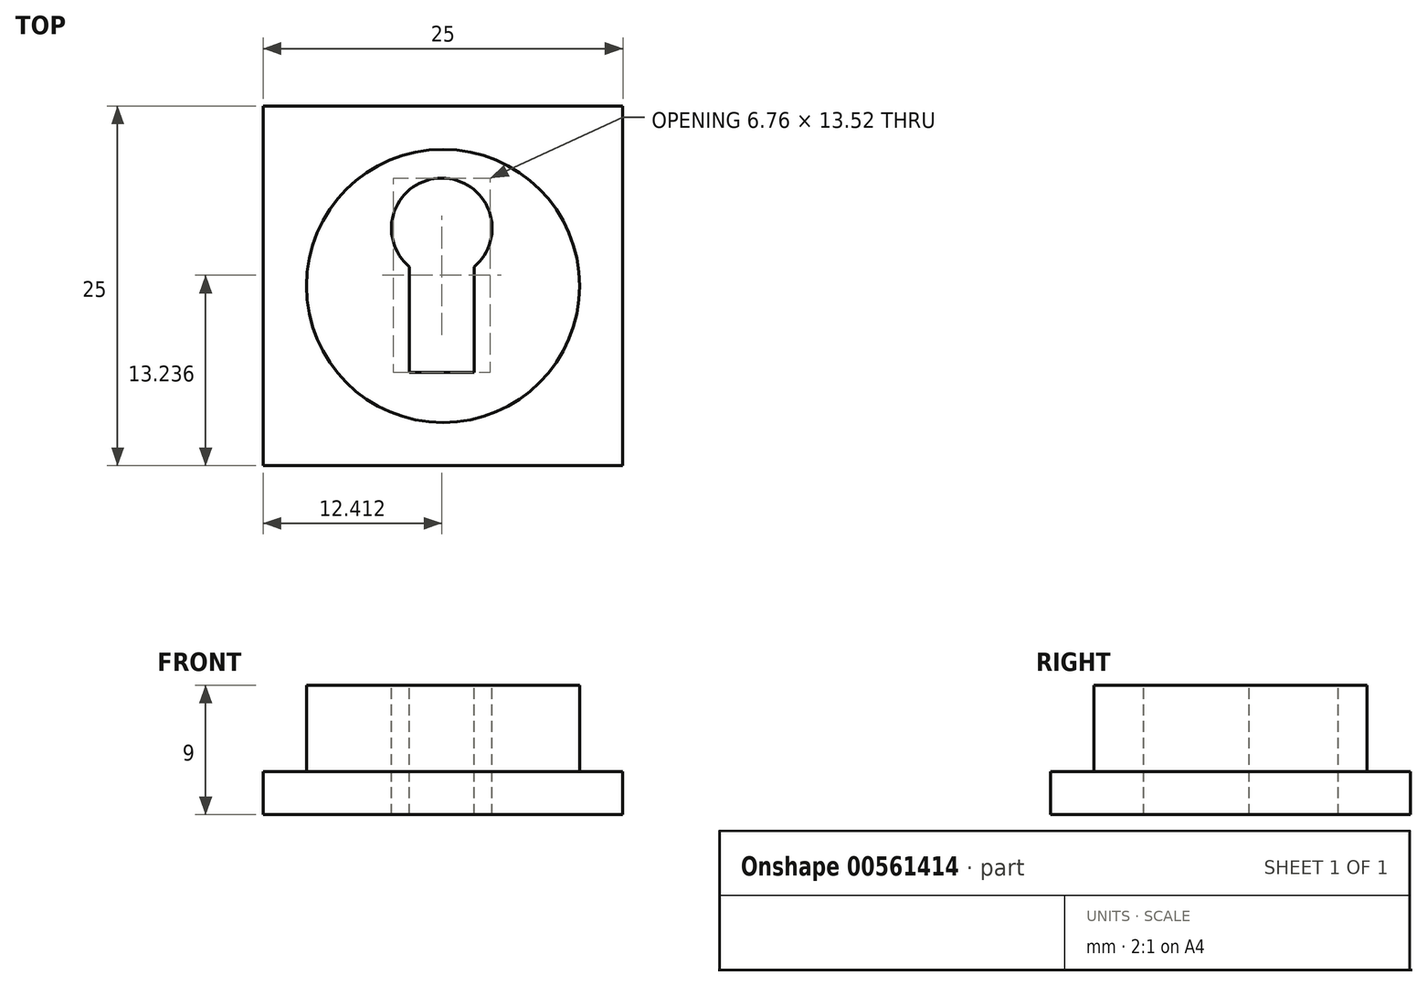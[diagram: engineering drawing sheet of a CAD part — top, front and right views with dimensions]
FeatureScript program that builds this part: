
annotation { "Feature Type Name" : "Feature", "Feature Type Description" : "" }
export const myFeature = defineFeature(function(context is Context, id is Id, definition is map)
    precondition{}
    {
        {
            var Q0;
            Q0=qCreatedBy(makeId("Top.planeOp"),FACE);
            var sketch = newSketch(context, id + "F0", { "sketchPlane" : qUnion([Q0])});
            skLineSegment(sketch, "E0.bottom", {"start": v(-56.28, 54.26) * mm, "end": v(-31.28, 54.26) * mm});
            skLineSegment(sketch, "E0.top", {"start": v(-56.28, 29.26) * mm, "end": v(-31.28, 29.26) * mm});
            skLineSegment(sketch, "E0.left", {"start": v(-56.28, 54.26) * mm, "end": v(-56.28, 29.26) * mm});
            skLineSegment(sketch, "E0.right", {"start": v(-31.28, 54.26) * mm, "end": v(-31.28, 29.26) * mm});
            skSolve(sketch);
        }
        {
            var Q0;
            Q0=makeQuery(id+"F0.imprint","IMPRINT",FACE,{"disambiguationData":[TD([[makeQuery(id+"F0.imprint","IMPRINT",EDGE,{"derivedFrom":sQuery(id+"F0.wireOp",EDGE,"E0.bottom")}),-1.0]])]});
            extrude(context, id + "F1", {"entities" : qUnion([Q0]), "depth" : 3 * mm, "offsetDistance" : 25 * mm});
        }
        {
            var Q0;
            Q0=makeQuery(id+"F1.opExtrude","CAP_FACE",FACE,{"disambiguationData":[OSD([sQuery(id+"F0.wireOp",EDGE,"E0.bottom"),sQuery(id+"F0.wireOp",EDGE,"E0.top"),sQuery(id+"F0.wireOp",EDGE,"E0.left"),sQuery(id+"F0.wireOp",EDGE,"E0.right")])],"isStart":false});
            var sketch = newSketch(context, id + "F2", { "sketchPlane" : qUnion([Q0])});
            skCircle(sketch, "E1", {"center": v(-43.78, 41.76) * mm, "radius": 9.5 * mm});
            skPoint(sketch, "E1.centerSnap0", {"position": v(-56.28, 41.76) * mm});
            skPoint(sketch, "E1.centerSnap1", {"position": v(-43.78, 54.26) * mm});
            skSolve(sketch);
        }
        {
            var Q0;
            Q0=makeQuery(id+"F2.imprint","IMPRINT",FACE,{"disambiguationData":[TD([[makeQuery(id+"F2.imprint","IMPRINT",EDGE,{"derivedFrom":sQuery(id+"F2.wireOp",EDGE,"E1")}),1.0]])]});
            extrude(context, id + "F3", {"entities" : qUnion([Q0]), "operationType" : NewBodyOperationType.ADD, "depth" : 6 * mm, "offsetDistance" : 25 * mm});
        }
        {
            var Q0;
            Q0=makeQuery(id+"F3.opExtrude","CAP_FACE",FACE,{"disambiguationData":[OSD([sQuery(id+"F2.wireOp",EDGE,"E1")])],"isStart":false});
            var sketch = newSketch(context, id + "F4", { "sketchPlane" : qUnion([Q0])});
            skLineSegment(sketch, "E2", {"start": v(-43.87, 73.13) * mm, "end": v(-43.87, 9.59) * mm, "construction": true});
            skLineSegment(sketch, "E3", {"start": v(-77.4, 41.36) * mm, "end": v(-11.9, 41.36) * mm});
            skPoint(sketch, "E3.startSnap0", {"position": v(-43.87, 41.36) * mm});
            skCircle(sketch, "E4", {"center": v(-43.87, 45.76) * mm, "radius": 3.5 * mm});
            skLineSegment(sketch, "E5.bottom", {"start": v(-46.12, 43.07) * mm, "end": v(-41.62, 43.07) * mm});
            skLineSegment(sketch, "E5.top", {"start": v(-46.12, 35.73) * mm, "end": v(-41.62, 35.73) * mm});
            skLineSegment(sketch, "E5.left", {"start": v(-46.12, 43.07) * mm, "end": v(-46.12, 35.73) * mm});
            skLineSegment(sketch, "E5.right", {"start": v(-41.62, 43.07) * mm, "end": v(-41.62, 35.73) * mm});
            skSolve(sketch);
        }
        {
            var Q0;
            {var subQ5=sQuery(id+"F4.wireOp",EDGE,"E5.top");Q0=makeQuery(id+"F4.imprint","IMPRINT",FACE,{"disambiguationData":[TD([[makeQuery(id+"F4.imprint","IMPRINT",EDGE,{"derivedFrom":subQ5}),1.0]])]});}
            var Q1;
            {var subQ0=sQuery(id+"F4.wireOp",EDGE,"E5.bottom");var subQ1=sQuery(id+"F4.wireOp",EDGE,"E4");var subQ3=makeQuery(id+"F4.imprint","INTERSECT",VERTEX,{"derivedFrom":[subQ1,subQ0]});Q1=makeQuery(id+"F4.imprint","IMPRINT",FACE,{"disambiguationData":[TD([[makeQuery(id+"F4.imprint","IMPRINT",EDGE,{"disambiguationData":[TD([[subQ3,1.0]])],"derivedFrom":subQ1}),1.0]])]});}
            var Q2;
            {var subQ0=sQuery(id+"F4.wireOp",EDGE,"E5.bottom");var subQ1=sQuery(id+"F4.wireOp",EDGE,"E4");var subQ3=makeQuery(id+"F4.imprint","INTERSECT",VERTEX,{"derivedFrom":[subQ1,subQ0]});Q2=makeQuery(id+"F4.imprint","IMPRINT",FACE,{"disambiguationData":[TD([[makeQuery(id+"F4.imprint","IMPRINT",EDGE,{"disambiguationData":[TD([[subQ3,1.0]])],"derivedFrom":subQ1}),1.0]])]});}
            var Q3;
            {var subQ0=sQuery(id+"F4.wireOp",EDGE,"E5.left");var subQ4=sQuery(id+"F4.wireOp",EDGE,"E3");var subQ5=makeQuery(id+"F4.imprint","INTERSECT",VERTEX,{"derivedFrom":[subQ4,subQ0]});Q3=makeQuery(id+"F4.imprint","IMPRINT",FACE,{"disambiguationData":[TD([[makeQuery(id+"F4.imprint","IMPRINT",EDGE,{"disambiguationData":[TD([[subQ5,-1.0]])],"derivedFrom":subQ4}),1.0]])]});}
            var Q4;
            {var subQ0=sQuery(id+"F4.wireOp",EDGE,"E5.bottom");var subQ1=sQuery(id+"F4.wireOp",EDGE,"E4");var subQ3=makeQuery(id+"F4.imprint","INTERSECT",VERTEX,{"derivedFrom":[subQ1,subQ0]});Q4=makeQuery(id+"F4.imprint","IMPRINT",FACE,{"disambiguationData":[TD([[makeQuery(id+"F4.imprint","IMPRINT",EDGE,{"disambiguationData":[TD([[subQ3,-1.0]])],"derivedFrom":subQ1}),1.0]])]});}
            extrude(context, id + "F5", {"entities" : qUnion([Q0, Q1, Q2, Q3, Q4]), "operationType" : NewBodyOperationType.REMOVE, "oppositeDirection" : true, "depth" : 9 * mm, "offsetDistance" : 25 * mm});
        }
    });
